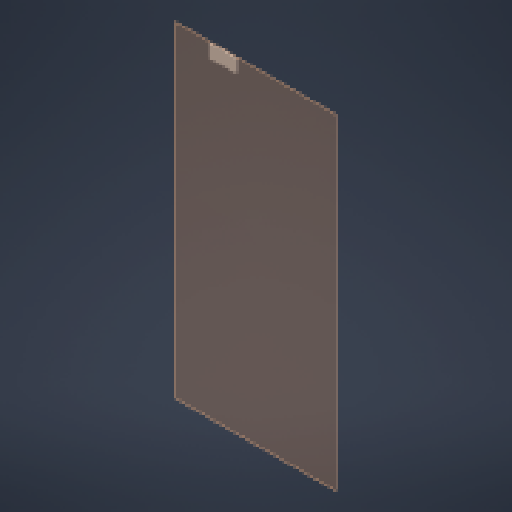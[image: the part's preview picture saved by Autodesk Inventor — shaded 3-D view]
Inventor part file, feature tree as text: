
AUTODESK INVENTOR PART (.ipt)
format: ipt  version: 2024 (Build 280153000, 153)  size: 125,952 bytes
history: native  units: mm
features: other x5, plane x1, extrude x1, sketch x1
ambient origin geometry x8: Origin, YZ Plane, XZ Plane, XY Plane, X Axis, Y Axis, Z Axis, Center Point
bodies: Body1 (feature_tree)
feature tree (8):
  other  "Sólido1"
  plane  "Plano de trabajo1"
  extrude  "Extrusión1"  Depth=30.0mm
  sketch  "Boceto1"  dims[d0=120.0mm d1=30.0mm d2=30.0mm d3=30.0mm d4=30.0mm d5=2.0mm d6=0.0mm]
  other  "<userpath>\Downloads\Piezas CMR\Marco_APM_002\Marco_apm_002-1.iam"
  other  "Marco_apm_002-1.iam"
  other  "Marco_Conveyor_Aereo:1"
  other  "Marco:1"
